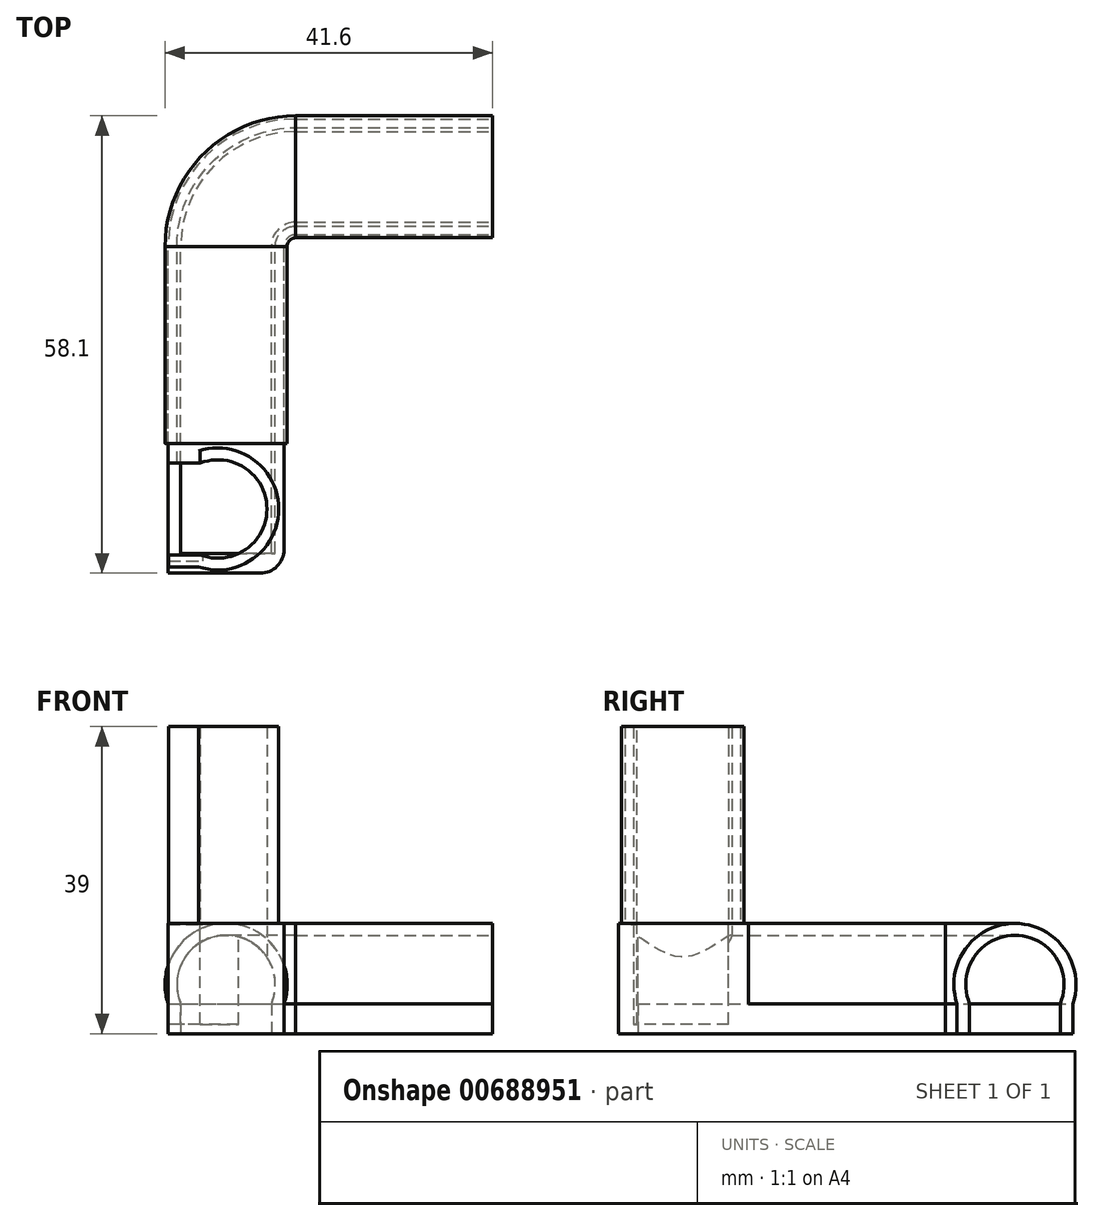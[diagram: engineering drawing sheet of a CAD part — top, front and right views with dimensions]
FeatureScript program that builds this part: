
annotation { "Feature Type Name" : "Feature", "Feature Type Description" : "" }
export const myFeature = defineFeature(function(context is Context, id is Id, definition is map)
    precondition{}
    {
        {
            var Q0;
            Q0=qCreatedBy(makeId("Front.planeOp"),FACE);
            var sketch = newSketch(context, id + "F0", { "sketchPlane" : qUnion([Q0])});
            skCircle(sketch, "E0", {"center": v(0, 0) * mm, "radius": 6.25 * mm});
            skCircle(sketch, "E1", {"center": v(0, 0) * mm, "radius": 7.75 * mm});
            skLineSegment(sketch, "E2", {"start": v(0, 0) * mm, "end": v(0, -7.75) * mm, "construction": true});
            skLineSegment(sketch, "E3", {"start": v(0, -2.45) * mm, "end": v(5.75, -2.45) * mm});
            skLineSegment(sketch, "E4", {"start": v(0, -2.45) * mm, "end": v(-5.75, -2.45) * mm});
            skLineSegment(sketch, "E5", {"start": v(5.75, -2.45) * mm, "end": v(5.75, -5.2) * mm});
            skLineSegment(sketch, "E6", {"start": v(-5.75, -2.45) * mm, "end": v(-5.75, -5.2) * mm});
            skLineSegment(sketch, "E7", {"start": v(5.75, -2.45) * mm, "end": v(7.35, -2.45) * mm, "construction": true});
            skLineSegment(sketch, "E8", {"start": v(-5.75, -2.45) * mm, "end": v(-7.35, -2.45) * mm, "construction": true});
            skLineSegment(sketch, "E9.bottom", {"start": v(-5.75, -2.45) * mm, "end": v(-7.35, -2.45) * mm});
            skLineSegment(sketch, "E9.top", {"start": v(-5.75, -7.75) * mm, "end": v(-7.35, -7.75) * mm});
            skLineSegment(sketch, "E9.left", {"start": v(-5.75, -2.45) * mm, "end": v(-5.75, -7.75) * mm});
            skLineSegment(sketch, "E9.right", {"start": v(-7.35, -2.45) * mm, "end": v(-7.35, -7.75) * mm});
            skLineSegment(sketch, "E10.bottom", {"start": v(5.75, -2.45) * mm, "end": v(7.35, -2.45) * mm});
            skLineSegment(sketch, "E10.top", {"start": v(5.75, -7.75) * mm, "end": v(7.35, -7.75) * mm});
            skLineSegment(sketch, "E10.left", {"start": v(5.75, -2.45) * mm, "end": v(5.75, -7.75) * mm});
            skLineSegment(sketch, "E10.right", {"start": v(7.35, -2.45) * mm, "end": v(7.35, -7.75) * mm});
            skLineSegment(sketch, "E11", {"start": v(0, -6.25) * mm, "end": v(-7.35, -6.25) * mm, "construction": true});
            skLineSegment(sketch, "E12", {"start": v(0, -6.25) * mm, "end": v(7.35, -6.25) * mm, "construction": true});
            skLineSegment(sketch, "E13", {"start": v(-7.35, -6.25) * mm, "end": v(-5.75, -6.25) * mm});
            skLineSegment(sketch, "E14", {"start": v(7.35, -6.25) * mm, "end": v(5.75, -6.25) * mm});
            skSolve(sketch);
        }
        {
            var Q0;
            {var subQ5=sQuery(id+"F0.wireOp",EDGE,"E13");Q0=makeQuery(id+"F0.imprint","IMPRINT",FACE,{"disambiguationData":[TD([[makeQuery(id+"F0.imprint","IMPRINT",EDGE,{"derivedFrom":subQ5}),1.0]])]});}
            var Q1;
            {var subQ5=sQuery(id+"F0.wireOp",EDGE,"E14");Q1=makeQuery(id+"F0.imprint","IMPRINT",FACE,{"disambiguationData":[TD([[makeQuery(id+"F0.imprint","IMPRINT",EDGE,{"derivedFrom":subQ5}),-1.0]])]});}
            var Q2;
            {var subQ2=sQuery(id+"F0.wireOp",EDGE,"E9.bottom");Q2=makeQuery(id+"F0.imprint","IMPRINT",FACE,{"disambiguationData":[TD([[makeQuery(id+"F0.imprint","IMPRINT",EDGE,{"derivedFrom":subQ2}),-1.0]])]});}
            var Q3;
            {var subQ0=sQuery(id+"F0.wireOp",EDGE,"E9.bottom");Q3=makeQuery(id+"F0.imprint","IMPRINT",FACE,{"disambiguationData":[TD([[makeQuery(id+"F0.imprint","IMPRINT",EDGE,{"derivedFrom":subQ0}),1.0]])]});}
            var Q4;
            {var subQ0=sQuery(id+"F0.wireOp",EDGE,"E10.bottom");Q4=makeQuery(id+"F0.imprint","IMPRINT",FACE,{"disambiguationData":[TD([[makeQuery(id+"F0.imprint","IMPRINT",EDGE,{"derivedFrom":subQ0}),-1.0]])]});}
            extrude(context, id + "F1", {"entities" : qUnion([Q0, Q1, Q2, Q3, Q4]), "depth" : 25 * mm, "offsetDistance" : 25 * mm});
        }
        {
            var Q0;
            Q0=makeQuery(id+"F1.opExtrude","SWEPT_BODY",BODY,{"disambiguationData":[OSD([sQuery(id+"F0.wireOp",EDGE,"E0"),sQuery(id+"F0.wireOp",EDGE,"E1"),sQuery(id+"F0.wireOp",EDGE,"E9.left"),sQuery(id+"F0.wireOp",EDGE,"E9.right"),sQuery(id+"F0.wireOp",EDGE,"E10.left"),sQuery(id+"F0.wireOp",EDGE,"E10.right"),sQuery(id+"F0.wireOp",EDGE,"E13"),sQuery(id+"F0.wireOp",EDGE,"E14")])]});
            var Q1;
            Q1=makeQuery(id+"F1.opExtrude","CAP_EDGE",EDGE,{"disambiguationData":[OSD([sQuery(id+"F0.wireOp",EDGE,"E10.right")])],"isStart":true});
            transform(context, id + "F2", {"entities" : qUnion([Q0]), "transformType" : TransformType.ROTATION, "transformAxis" : qUnion([Q1]), "angle" : 90 * degree, "makeCopy" : true});
        }
        {
            var Q0;
            Q0=makeQuery(id+"F2.opPattern","COPY",BODY,{"derivedFrom":makeQuery(id+"F1.opExtrude","SWEPT_BODY",BODY,{"disambiguationData":[OSD([sQuery(id+"F0.wireOp",EDGE,"E0"),sQuery(id+"F0.wireOp",EDGE,"E1"),sQuery(id+"F0.wireOp",EDGE,"E9.left"),sQuery(id+"F0.wireOp",EDGE,"E9.right"),sQuery(id+"F0.wireOp",EDGE,"E10.left"),sQuery(id+"F0.wireOp",EDGE,"E10.right"),sQuery(id+"F0.wireOp",EDGE,"E13"),sQuery(id+"F0.wireOp",EDGE,"E14")])]}),"instanceName":"1"});
            transform(context, id + "F3", {"entities" : qUnion([Q0]), "transformType" : TransformType.TRANSLATION_3D, "dx" : 26.5 * mm, "dy" : 1.5 * mm, "dz" : 0 * mm, "makeCopy" : false});
        }
        {
            var Q0;
            Q0=makeQuery(id+"F2.opPattern","COPY",FACE,{"derivedFrom":makeQuery(id+"F1.opExtrude","SWEPT_FACE",FACE,{"disambiguationData":[OSD([sQuery(id+"F0.wireOp",EDGE,"E13")])]}),"instanceName":"1"});
            var sketch = newSketch(context, id + "F4", { "sketchPlane" : qUnion([Q0])});
            skPoint(sketch, "E15.first.point", {"position": v(8.85, -14.6) * mm});
            skPoint(sketch, "E15.second.point", {"position": v(-5.75, 0) * mm});
            skPoint(sketch, "E15.third.point", {"position": v(-3.46, -7.86) * mm});
            skArc(sketch, "E16", {"start": v(-5.75, 0) * mm, "mid": v(-1.47, -10.33) * mm, "end": v(8.85, -14.6) * mm});
            skSolve(sketch);
        }
        {
            var Q0;
            Q0=makeQuery(id+"F2.opPattern","COPY",FACE,{"derivedFrom":makeQuery(id+"F1.opExtrude","CAP_FACE",FACE,{"disambiguationData":[OSD([sQuery(id+"F0.wireOp",EDGE,"E0"),sQuery(id+"F0.wireOp",EDGE,"E1"),sQuery(id+"F0.wireOp",EDGE,"E9.left"),sQuery(id+"F0.wireOp",EDGE,"E9.right"),sQuery(id+"F0.wireOp",EDGE,"E10.left"),sQuery(id+"F0.wireOp",EDGE,"E10.right"),sQuery(id+"F0.wireOp",EDGE,"E13"),sQuery(id+"F0.wireOp",EDGE,"E14")])],"isStart":false}),"instanceName":"1"});
            var Q1;
            Q1=makeQuery(id+"F1.opExtrude","CAP_FACE",FACE,{"disambiguationData":[OSD([sQuery(id+"F0.wireOp",EDGE,"E0"),sQuery(id+"F0.wireOp",EDGE,"E1"),sQuery(id+"F0.wireOp",EDGE,"E9.left"),sQuery(id+"F0.wireOp",EDGE,"E9.right"),sQuery(id+"F0.wireOp",EDGE,"E10.left"),sQuery(id+"F0.wireOp",EDGE,"E10.right"),sQuery(id+"F0.wireOp",EDGE,"E13"),sQuery(id+"F0.wireOp",EDGE,"E14")])],"isStart":true});
            var Q2;
            Q2=sQuery(id+"F4.wireOp",EDGE,"E16");
            sweep(context, id + "F5", {"profiles" : qUnion([Q0, Q1]), "path" : qUnion([Q2])});
        }
        {
            var Q0;
            {var subQ0=sQuery(id+"F4.wireOp",EDGE,"E16");var subQ1=sQuery(id+"F0.wireOp",EDGE,"E14");var subQ2=sQuery(id+"F0.wireOp",EDGE,"E13");var subQ3=sQuery(id+"F0.wireOp",EDGE,"E10.right");var subQ4=sQuery(id+"F0.wireOp",EDGE,"E10.left");var subQ5=sQuery(id+"F0.wireOp",EDGE,"E9.right");var subQ6=sQuery(id+"F0.wireOp",EDGE,"E9.left");var subQ7=sQuery(id+"F0.wireOp",EDGE,"E1");var subQ8=sQuery(id+"F0.wireOp",EDGE,"E0");Q0=makeQuery(id+"F5.opSweep","SWEPT_BODY",BODY,{"disambiguationData":[OSD([subQ8,subQ7,subQ6,subQ5,subQ4,subQ3,subQ2,subQ1,subQ0]),TDD([makeQuery(id+"F2.opPattern","COPY",FACE,{"derivedFrom":makeQuery(id+"F1.opExtrude","CAP_FACE",FACE,{"disambiguationData":[OSD([subQ8,subQ7,subQ6,subQ5,subQ4,subQ3,subQ2,subQ1])],"isStart":false}),"instanceName":"1"}),subQ0])]});}
            deleteBodies(context, id + "F6", {"entities" : qUnion([Q0])});
        }
        {
            var Q0;
            Q0=makeQuery(id+"F1.opExtrude","SWEPT_BODY",BODY,{"disambiguationData":[OSD([sQuery(id+"F0.wireOp",EDGE,"E0"),sQuery(id+"F0.wireOp",EDGE,"E1"),sQuery(id+"F0.wireOp",EDGE,"E9.left"),sQuery(id+"F0.wireOp",EDGE,"E9.right"),sQuery(id+"F0.wireOp",EDGE,"E10.left"),sQuery(id+"F0.wireOp",EDGE,"E10.right"),sQuery(id+"F0.wireOp",EDGE,"E13"),sQuery(id+"F0.wireOp",EDGE,"E14")])]});
            var Q1;
            Q1=makeQuery(id+"F1.opExtrude","CAP_EDGE",EDGE,{"disambiguationData":[OSD([sQuery(id+"F0.wireOp",EDGE,"E13")])],"isStart":false});
            transform(context, id + "F7", {"entities" : qUnion([Q0]), "transformType" : TransformType.ROTATION, "transformAxis" : qUnion([Q1]), "angle" : 90 * degree, "oppositeDirection" : true, "makeCopy" : true});
        }
        {
            var Q0;
            Q0=makeQuery(id+"F7.opPattern","COPY",BODY,{"derivedFrom":makeQuery(id+"F1.opExtrude","SWEPT_BODY",BODY,{"disambiguationData":[OSD([sQuery(id+"F0.wireOp",EDGE,"E0"),sQuery(id+"F0.wireOp",EDGE,"E1"),sQuery(id+"F0.wireOp",EDGE,"E9.left"),sQuery(id+"F0.wireOp",EDGE,"E9.right"),sQuery(id+"F0.wireOp",EDGE,"E10.left"),sQuery(id+"F0.wireOp",EDGE,"E10.right"),sQuery(id+"F0.wireOp",EDGE,"E13"),sQuery(id+"F0.wireOp",EDGE,"E14")])]}),"instanceName":"1"});
            transform(context, id + "F8", {"entities" : qUnion([Q0]), "transformType" : TransformType.TRANSLATION_3D, "dx" : 0 * mm, "dy" : -14.7 * mm, "dz" : 42.9 * mm, "makeCopy" : false});
        }
        {
            var Q0;
            Q0=makeQuery(id+"F7.opPattern","COPY",BODY,{"derivedFrom":makeQuery(id+"F1.opExtrude","SWEPT_BODY",BODY,{"disambiguationData":[OSD([sQuery(id+"F0.wireOp",EDGE,"E0"),sQuery(id+"F0.wireOp",EDGE,"E1"),sQuery(id+"F0.wireOp",EDGE,"E9.left"),sQuery(id+"F0.wireOp",EDGE,"E9.right"),sQuery(id+"F0.wireOp",EDGE,"E10.left"),sQuery(id+"F0.wireOp",EDGE,"E10.right"),sQuery(id+"F0.wireOp",EDGE,"E13"),sQuery(id+"F0.wireOp",EDGE,"E14")])]}),"instanceName":"1"});
            var Q1;
            Q1=makeQuery(id+"F7.opPattern","COPY",EDGE,{"derivedFrom":makeQuery(id+"F1.opExtrude","SWEPT_EDGE",EDGE,{"disambiguationData":[OSD([sQuery(id+"F0.wireOp",EDGE,"E10.right"),sQuery(id+"F0.wireOp",EDGE,"E14")])]}),"instanceName":"1"});
            transform(context, id + "F9", {"entities" : qUnion([Q0]), "transformType" : TransformType.ROTATION, "transformAxis" : qUnion([Q1]), "angle" : 90 * degree, "makeCopy" : false});
        }
        {
            var Q0;
            Q0=makeQuery(id+"F7.opPattern","COPY",BODY,{"derivedFrom":makeQuery(id+"F1.opExtrude","SWEPT_BODY",BODY,{"disambiguationData":[OSD([sQuery(id+"F0.wireOp",EDGE,"E0"),sQuery(id+"F0.wireOp",EDGE,"E1"),sQuery(id+"F0.wireOp",EDGE,"E9.left"),sQuery(id+"F0.wireOp",EDGE,"E9.right"),sQuery(id+"F0.wireOp",EDGE,"E10.left"),sQuery(id+"F0.wireOp",EDGE,"E10.right"),sQuery(id+"F0.wireOp",EDGE,"E13"),sQuery(id+"F0.wireOp",EDGE,"E14")])]}),"instanceName":"1"});
            transform(context, id + "F10", {"entities" : qUnion([Q0]), "transformType" : TransformType.TRANSLATION_3D, "dx" : -14.66 * mm, "dy" : -1 * mm, "dz" : -3.9 * mm, "makeCopy" : false});
        }
        {
            var Q0;
            Q0=makeQuery(id+"F1.opExtrude","CAP_FACE",FACE,{"disambiguationData":[OSD([sQuery(id+"F0.wireOp",EDGE,"E0"),sQuery(id+"F0.wireOp",EDGE,"E1"),sQuery(id+"F0.wireOp",EDGE,"E9.left"),sQuery(id+"F0.wireOp",EDGE,"E9.right"),sQuery(id+"F0.wireOp",EDGE,"E10.left"),sQuery(id+"F0.wireOp",EDGE,"E10.right"),sQuery(id+"F0.wireOp",EDGE,"E13"),sQuery(id+"F0.wireOp",EDGE,"E14")])],"isStart":false});
            var sketch = newSketch(context, id + "F11", { "sketchPlane" : qUnion([Q0])});
            skPoint(sketch, "E17.oppositeSnap0", {"position": v(0, 7.75) * mm});
            skLineSegment(sketch, "E17.bottom", {"start": v(-7.35, -6.25) * mm, "end": v(7.35, -6.25) * mm});
            skLineSegment(sketch, "E17.top", {"start": v(-7.35, 7.75) * mm, "end": v(7.35, 7.75) * mm});
            skLineSegment(sketch, "E17.left", {"start": v(-7.35, -6.25) * mm, "end": v(-7.35, 7.75) * mm});
            skLineSegment(sketch, "E17.right", {"start": v(7.35, -6.25) * mm, "end": v(7.35, 7.75) * mm});
            skSolve(sketch);
        }
        {
            var Q0;
            Q0 = qSketchRegion(id + "F11", true);
            extrude(context, id + "F12", {"entities" : qUnion([Q0]), "operationType" : NewBodyOperationType.ADD, "depth" : 16.5 * mm, "offsetDistance" : 25 * mm});
        }
        {
            var Q0;
            {var subQ0=sQuery(id+"F11.wireOp",EDGE,"E17.bottom");Q0=makeQuery(id+"F12.boolean.opBoolean","SPLIT",FACE,{"disambiguationData":[TD([makeQuery(id+"F1.opExtrude","SWEPT_FACE",FACE,{"disambiguationData":[OSD([sQuery(id+"F0.wireOp",EDGE,"E0")])]})])],"derivedFrom":makeQuery(id+"F12.opExtrude","CAP_FACE",FACE,{"disambiguationData":[OSD([subQ0,sQuery(id+"F11.wireOp",EDGE,"E17.top"),sQuery(id+"F11.wireOp",EDGE,"E17.left"),sQuery(id+"F11.wireOp",EDGE,"E17.right")])],"isStart":true})});}
            extrude(context, id + "F13", {"entities" : qUnion([Q0]), "operationType" : NewBodyOperationType.REMOVE, "oppositeDirection" : true, "depth" : 14 * mm, "offsetDistance" : 25 * mm});
        }
        {
            var Q0;
            Q0=makeQuery(id+"F12.opExtrude","SWEPT_FACE",FACE,{"disambiguationData":[OSD([sQuery(id+"F11.wireOp",EDGE,"E17.top")])]});
            var sketch = newSketch(context, id + "F14", { "sketchPlane" : qUnion([Q0])});
            skCircle(sketch, "E18", {"center": v(-1.05, -33.35) * mm, "radius": 6.11 * mm});
            skPoint(sketch, "E18.first.point", {"position": v(-2.8, -27.5) * mm});
            skPoint(sketch, "E18.second.point", {"position": v(-3.3, -39.03) * mm});
            skPoint(sketch, "E18.third.point", {"position": v(5.05, -33.02) * mm});
            skLineSegment(sketch, "E19.bottom", {"start": v(-7.35, -28.42) * mm, "end": v(-3, -28.42) * mm});
            skLineSegment(sketch, "E19.top", {"start": v(-7.35, -39.93) * mm, "end": v(-3, -39.93) * mm});
            skLineSegment(sketch, "E19.left", {"start": v(-7.35, -28.42) * mm, "end": v(-7.35, -39.93) * mm});
            skLineSegment(sketch, "E19.right", {"start": v(-3, -28.42) * mm, "end": v(-3, -39.93) * mm});
            skSolve(sketch);
        }
        {
            var Q0;
            Q0 = qSketchRegion(id + "F14", true);
            extrude(context, id + "F15", {"entities" : qUnion([Q0]), "operationType" : NewBodyOperationType.REMOVE, "oppositeDirection" : true, "depth" : .1 * mm, "offsetDistance" : 25 * mm});
        }
        {
            var Q0;
            Q0=makeQuery(id+"F12.opExtrude","CAP_EDGE",EDGE,{"disambiguationData":[OSD([sQuery(id+"F11.wireOp",EDGE,"E17.right")])],"isStart":false});
            fillet(context, id + "F16", {"entities" : qUnion([Q0]), "radius" : 3 * mm, "tangentPropagation" : true, "allowEdgeOverflow" : false});
        }
        {
            var Q0;
            Q0=makeQuery(id+"F7.opPattern","COPY",FACE,{"derivedFrom":makeQuery(id+"F1.opExtrude","SWEPT_FACE",FACE,{"disambiguationData":[OSD([sQuery(id+"F0.wireOp",EDGE,"E14")])]}),"instanceName":"1"});
            var sketch = newSketch(context, id + "F17", { "sketchPlane" : qUnion([Q0])});
            skSolve(sketch);
        }
        {
            var Q0;
            {var subQ0=sQuery(id+"F0.wireOp",EDGE,"E14");Q0=makeQuery(id+"F17.imprint","IMPRINT",FACE,{"disambiguationData":[TD([[makeQuery(id+"F17.imprint","IMPRINT",EDGE,{"derivedFrom":makeQuery(id+"F7.opPattern","COPY",EDGE,{"derivedFrom":makeQuery(id+"F1.opExtrude","CAP_EDGE",EDGE,{"disambiguationData":[OSD([subQ0])],"isStart":true}),"instanceName":"1"})}),-1.0]])]});}
            var Q1;
            Q1=makeQuery(id+"F7.opPattern","COPY",FACE,{"derivedFrom":makeQuery(id+"F1.opExtrude","SWEPT_FACE",FACE,{"disambiguationData":[OSD([sQuery(id+"F0.wireOp",EDGE,"E13")])]}),"instanceName":"1"});
            extrude(context, id + "F18", {"entities" : qUnion([Q0, Q1]), "operationType" : NewBodyOperationType.REMOVE, "oppositeDirection" : true, "depth" : 4 * mm, "offsetDistance" : 25 * mm});
        }
        {
            var Q0;
            Q0=makeQuery(id+"F7.opPattern","COPY",FACE,{"derivedFrom":makeQuery(id+"F1.opExtrude","CAP_FACE",FACE,{"disambiguationData":[OSD([sQuery(id+"F0.wireOp",EDGE,"E0"),sQuery(id+"F0.wireOp",EDGE,"E1"),sQuery(id+"F0.wireOp",EDGE,"E9.left"),sQuery(id+"F0.wireOp",EDGE,"E9.right"),sQuery(id+"F0.wireOp",EDGE,"E10.left"),sQuery(id+"F0.wireOp",EDGE,"E10.right"),sQuery(id+"F0.wireOp",EDGE,"E13"),sQuery(id+"F0.wireOp",EDGE,"E14")])],"isStart":false}),"instanceName":"1"});
            var sketch = newSketch(context, id + "F19", { "sketchPlane" : qUnion([Q0])});
            skCircle(sketch, "E20", {"center": v(-1.06, -33.35) * mm, "radius": 6.25 * mm});
            skPoint(sketch, "E20.first.point", {"position": v(-3.3, -39.18) * mm});
            skPoint(sketch, "E20.second.point", {"position": v(-3.3, -27.52) * mm});
            skPoint(sketch, "E20.third.point", {"position": v(5.15, -32.6) * mm});
            skLineSegment(sketch, "E21.bottom", {"start": v(-3.3, -27.52) * mm, "end": v(-7.74, -27.52) * mm});
            skLineSegment(sketch, "E21.top", {"start": v(-3.3, -39.18) * mm, "end": v(-7.74, -39.18) * mm});
            skLineSegment(sketch, "E21.left", {"start": v(-3.3, -27.52) * mm, "end": v(-3.3, -39.18) * mm});
            skLineSegment(sketch, "E21.right", {"start": v(-7.74, -27.52) * mm, "end": v(-7.74, -39.18) * mm});
            skSolve(sketch);
        }
        {
            var Q0;
            Q0 = qSketchRegion(id + "F19", true);
            extrude(context, id + "F20", {"entities" : qUnion([Q0]), "operationType" : NewBodyOperationType.REMOVE, "oppositeDirection" : true, "depth" : 37.8 * mm, "offsetDistance" : 25 * mm});
        }
    });
